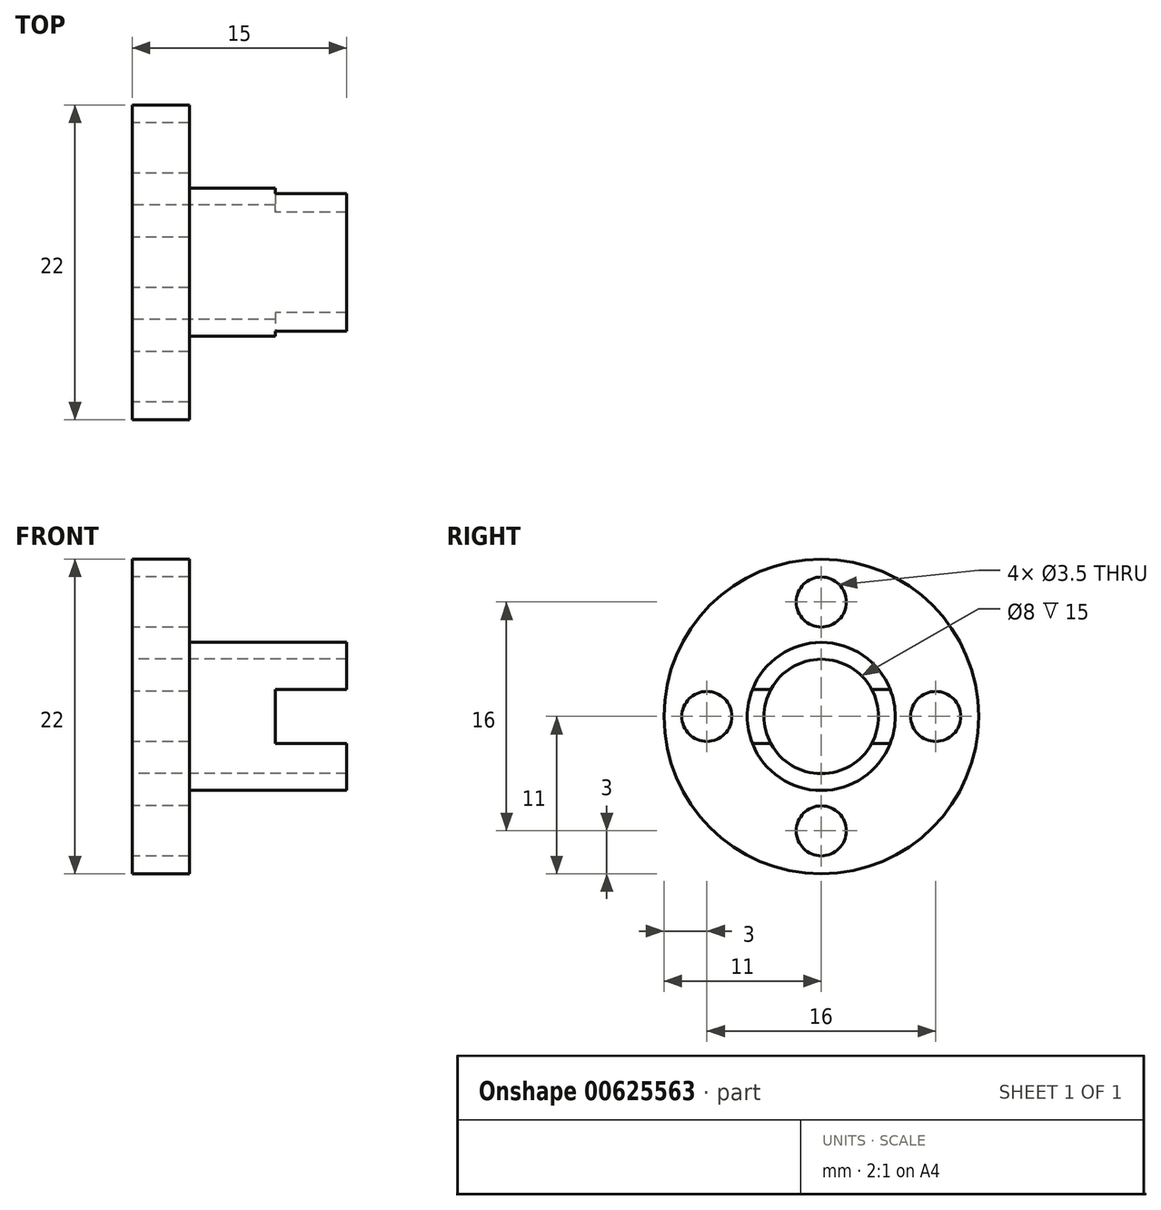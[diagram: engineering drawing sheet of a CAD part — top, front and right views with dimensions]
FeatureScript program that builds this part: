
annotation { "Feature Type Name" : "Feature", "Feature Type Description" : "" }
export const myFeature = defineFeature(function(context is Context, id is Id, definition is map)
    precondition{}
    {
        {
            var Q0;
            Q0=qCreatedBy(makeId("Top.planeOp"),FACE);
            var sketch = newSketch(context, id + "F0", { "sketchPlane" : qUnion([Q0])});
            skLineSegment(sketch, "E0", {"start": v(0, 11) * mm, "end": v(0, 4) * mm});
            skLineSegment(sketch, "E1", {"start": v(0, 11) * mm, "end": v(4, 11) * mm});
            skLineSegment(sketch, "E2", {"start": v(4, 11) * mm, "end": v(4, 5.17) * mm});
            skLineSegment(sketch, "E3", {"start": v(4, 5.17) * mm, "end": v(15, 5.18) * mm});
            skLineSegment(sketch, "E4", {"start": v(15, 5.18) * mm, "end": v(15, 4) * mm});
            skLineSegment(sketch, "E5", {"start": v(0, 4) * mm, "end": v(15, 4) * mm});
            skLineSegment(sketch, "E6", {"start": v(0, 0) * mm, "end": v(15, 0) * mm, "construction": true});
            skLineSegment(sketch, "E7", {"start": v(0, 4) * mm, "end": v(0, 0) * mm, "construction": true});
            skLineSegment(sketch, "E8", {"start": v(15, 4) * mm, "end": v(15, 0) * mm, "construction": true});
            skSolve(sketch);
        }
        {
            var Q0;
            Q0=qCreatedBy(makeId("Top.planeOp"),FACE);
            var sketch = newSketch(context, id + "F1", { "sketchPlane" : qUnion([Q0])});
            skLineSegment(sketch, "E9", {"start": v(0, 0) * mm, "end": v(15, 0) * mm, "construction": true});
            skSolve(sketch);
        }
        {
            var Q0;
            Q0 = qSketchRegion(id + "F0", true);
            var Q1;
            Q1=sQuery(id+"F0.wireOp",EDGE,"E6");
            revolve(context, id + "F2", {"surfaceOperationType" : NewSurfaceOperationType.NEW, "entities" : qUnion([Q0]), "axis" : qUnion([Q1]), "revolveType" : RevolveType.FULL});
        }
        {
            var Q0;
            Q0=makeQuery(id+"F2.opRevolve","SWEPT_FACE",FACE,{"disambiguationData":[OSD([sQuery(id+"F0.wireOp",EDGE,"E0")])]});
            var sketch = newSketch(context, id + "F3", { "sketchPlane" : qUnion([Q0])});
            skLineSegment(sketch, "E10", {"start": v(0, 0) * mm, "end": v(0, 8) * mm, "construction": true});
            skCircle(sketch, "E11", {"center": v(0, 8) * mm, "radius": 1.75 * mm});
            skLineSegment(sketch, "E12.1.0", {"start": v(0, 0) * mm, "end": v(-8, 0) * mm, "construction": true});
            skCircle(sketch, "E12.1.1", {"center": v(-8, 0) * mm, "radius": 1.75 * mm});
            skLineSegment(sketch, "E12.2.0", {"start": v(0, 0) * mm, "end": v(0, -8) * mm, "construction": true});
            skCircle(sketch, "E12.2.1", {"center": v(0, -8) * mm, "radius": 1.75 * mm});
            skLineSegment(sketch, "E12.3.0", {"start": v(0, 0) * mm, "end": v(8, 0) * mm, "construction": true});
            skCircle(sketch, "E12.3.1", {"center": v(8, 0) * mm, "radius": 1.75 * mm});
            skPoint(sketch, "E12.center", {"position": v(0, 0) * mm});
            skSolve(sketch);
        }
        {
            var Q0;
            Q0 = qSketchRegion(id + "F3", true);
            extrude(context, id + "F4", {"entities" : qUnion([Q0]), "operationType" : NewBodyOperationType.REMOVE, "endBound" : BoundingType.UP_TO_NEXT, "oppositeDirection" : true, "depth" : 25 * mm, "offsetDistance" : 25 * mm});
        }
        {
            var Q0;
            Q0=qCreatedBy(makeId("Front.planeOp"),FACE);
            var sketch = newSketch(context, id + "F5", { "sketchPlane" : qUnion([Q0])});
            skLineSegment(sketch, "E13", {"start": v(15, 0) * mm, "end": v(0, 0) * mm, "construction": true});
            skLineSegment(sketch, "E14.bottom", {"start": v(15, 1.9) * mm, "end": v(10, 1.9) * mm});
            skLineSegment(sketch, "E14.top", {"start": v(15, -1.9) * mm, "end": v(10, -1.9) * mm});
            skLineSegment(sketch, "E14.left", {"start": v(15, 1.9) * mm, "end": v(15, -1.9) * mm});
            skLineSegment(sketch, "E14.right", {"start": v(10, 1.9) * mm, "end": v(10, -1.9) * mm});
            skPoint(sketch, "E14.middle", {"position": v(12.5, 0) * mm});
            skSolve(sketch);
        }
        {
            var Q0;
            Q0 = qSketchRegion(id + "F5", true);
            extrude(context, id + "F6", {"entities" : qUnion([Q0]), "operationType" : NewBodyOperationType.REMOVE, "oppositeDirection" : true, "depth" : 15 * mm, "offsetDistance" : 25 * mm, "symmetric" : true});
        }
    });
